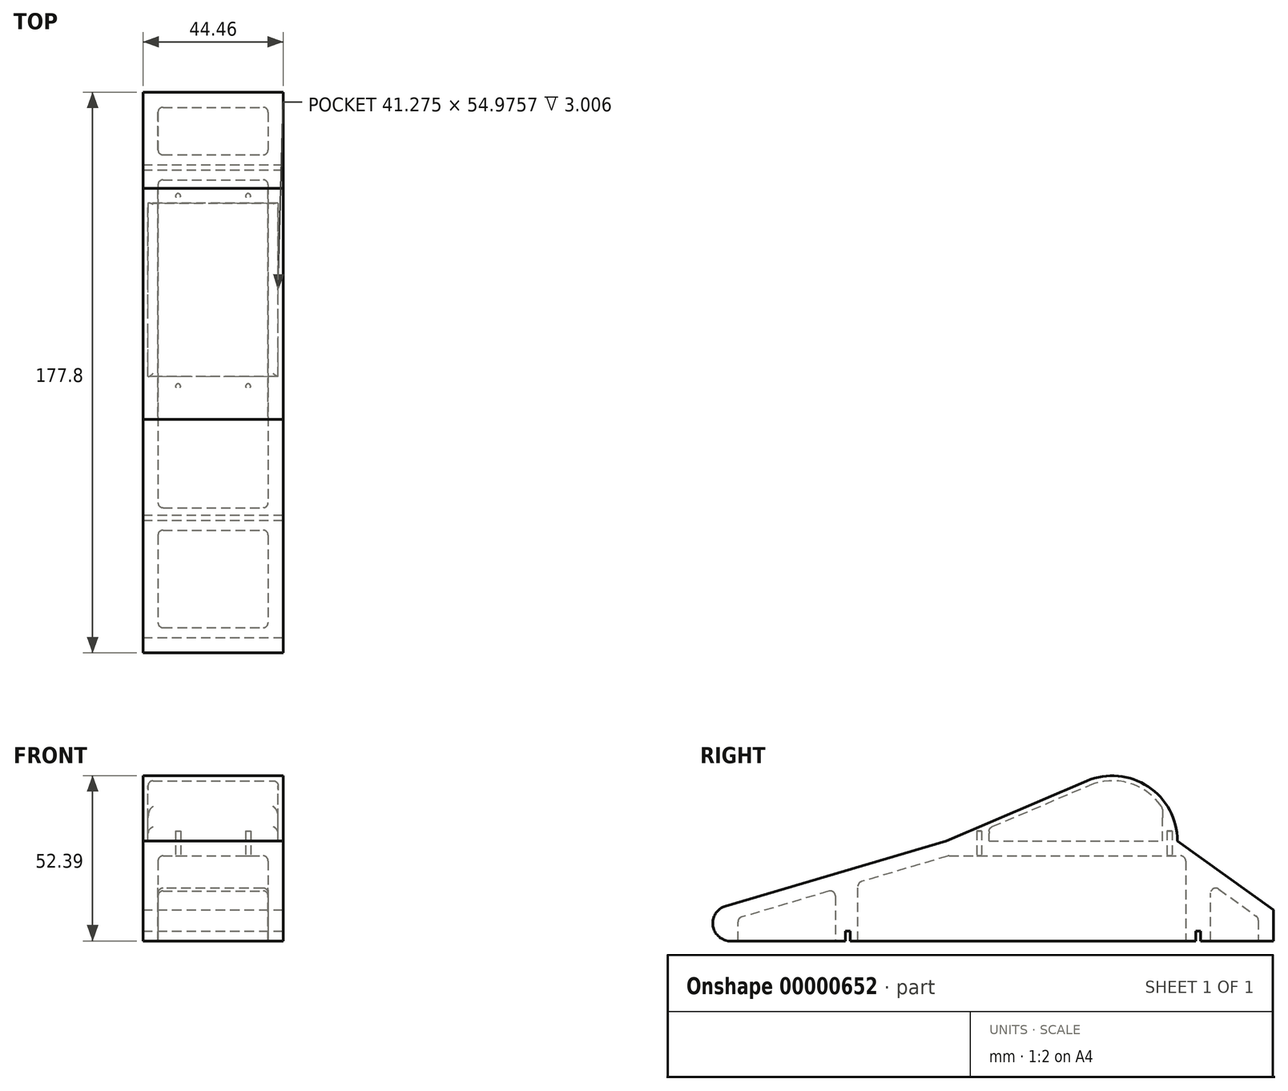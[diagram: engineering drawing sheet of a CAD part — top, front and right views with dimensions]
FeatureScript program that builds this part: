
annotation { "Feature Type Name" : "Feature", "Feature Type Description" : "" }
export const myFeature = defineFeature(function(context is Context, id is Id, definition is map)
    precondition{}
    {
        {
            var Q0;
            Q0=qCreatedBy(makeId("Right.planeOp"),FACE);
            var sketch = newSketch(context, id + "F0", { "sketchPlane" : qUnion([Q0])});
            skLineSegment(sketch, "E0.rect.bottom", {"start": v(-88.9, 15.88) * mm, "end": v(88.9, 15.88) * mm});
            skLineSegment(sketch, "E0.rect.top", {"start": v(-88.9, -15.88) * mm, "end": v(88.9, -15.88) * mm});
            skLineSegment(sketch, "E0.rect.left", {"start": v(-88.9, 15.88) * mm, "end": v(-88.9, -15.88) * mm});
            skLineSegment(sketch, "E0.rect.right", {"start": v(88.9, 15.88) * mm, "end": v(88.9, -15.88) * mm});
            skPoint(sketch, "E0.rect.middle", {"position": v(0, 0) * mm});
            skSolve(sketch);
        }
        {
            var Q0;
            Q0=makeQuery(id+"F0.imprint","IMPRINT",FACE,{"disambiguationData":[TD([[makeQuery(id+"F0.imprint","IMPRINT",EDGE,{"derivedFrom":sQuery(id+"F0.wireOp",EDGE,"E0.rect.bottom")}),-1.0]])]});
            extrude(context, id + "F1", {"entities" : qUnion([Q0]), "endBound" : BoundingType.SYMMETRIC, "depth" : 44.45 * mm});
        }
        {
            var Q0;
            Q0=qCreatedBy(makeId("Right.planeOp"),FACE);
            var sketch = newSketch(context, id + "F2", { "sketchPlane" : qUnion([Q0])});
            skLineSegment(sketch, "E1.bottom", {"start": v(-46.83, -15.88) * mm, "end": v(-45.24, -15.88) * mm});
            skLineSegment(sketch, "E1.top", {"start": v(-46.83, -12.7) * mm, "end": v(-45.24, -12.7) * mm});
            skLineSegment(sketch, "E1.left", {"start": v(-46.83, -15.87) * mm, "end": v(-46.83, -12.7) * mm});
            skLineSegment(sketch, "E1.right", {"start": v(-45.24, -15.87) * mm, "end": v(-45.24, -12.7) * mm});
            skLineSegment(sketch, "E2", {"start": v(-46.04, -12.7) * mm, "end": v(-46.04, -4.16) * mm, "construction": true});
            skLineSegment(sketch, "E3.bottom", {"start": v(64.3, -15.88) * mm, "end": v(65.88, -15.88) * mm});
            skLineSegment(sketch, "E3.top", {"start": v(64.3, -12.7) * mm, "end": v(65.88, -12.7) * mm});
            skLineSegment(sketch, "E3.left", {"start": v(64.3, -15.88) * mm, "end": v(64.3, -12.7) * mm});
            skLineSegment(sketch, "E3.right", {"start": v(65.88, -15.88) * mm, "end": v(65.88, -12.7) * mm});
            skCircle(sketch, "E4", {"center": v(-46.04, -13.7) * mm, "radius": 1 * mm, "construction": true});
            skCircle(sketch, "E5", {"center": v(65.09, -13.7) * mm, "radius": 1 * mm, "construction": true});
            skLineSegment(sketch, "E6", {"start": v(65.09, -13.7) * mm, "end": v(65.09, -12.7) * mm});
            skSolve(sketch);
        }
        {
            var Q0;
            {Q0=qUnion([makeQuery(id+"F2.imprint","IMPRINT",FACE,{"disambiguationData":[TD([[makeQuery(id+"F2.imprint","IMPRINT",EDGE,{"derivedFrom":sQuery(id+"F2.wireOp",EDGE,"E1.bottom")}),1.0]])]}),makeQuery(id+"F2.imprint","IMPRINT",FACE,{"disambiguationData":[TD([[makeQuery(id+"F2.imprint","IMPRINT",EDGE,{"derivedFrom":sQuery(id+"F2.wireOp",EDGE,"E3.bottom")}),1.0]])]})]);}
            extrude(context, id + "F3", {"entities" : qUnion([Q0]), "operationType" : NewBodyOperationType.REMOVE, "endBound" : BoundingType.SYMMETRIC, "oppositeDirection" : true, "depth" : 50.8 * mm});
        }
        {
            var Q0;
            Q0=qCreatedBy(makeId("Right.planeOp"),FACE);
            var sketch = newSketch(context, id + "F4", { "sketchPlane" : qUnion([Q0])});
            skLineSegment(sketch, "E7", {"start": v(-14.84, 15.88) * mm, "end": v(-84.87, -4.86) * mm});
            skArc(sketch, "E8", {"start": v(-84.87, -4.86) * mm, "mid": v(-88.9, -10.25) * mm, "end": v(-84.87, -15.64) * mm});
            skLineSegment(sketch, "E9", {"start": v(-14.84, 15.88) * mm, "end": v(-88.9, 15.88) * mm});
            skLineSegment(sketch, "E10", {"start": v(-88.9, 15.87) * mm, "end": v(-88.9, -15.88) * mm});
            skLineSegment(sketch, "E11", {"start": v(-84.87, -15.64) * mm, "end": v(-84.1, -15.88) * mm});
            skLineSegment(sketch, "E12", {"start": v(-84.1, -15.88) * mm, "end": v(-88.9, -15.88) * mm});
            skSolve(sketch);
        }
        {
            var Q0;
            Q0 = qSketchRegion(id + "F4", true);
            extrude(context, id + "F5", {"entities" : qUnion([Q0]), "operationType" : NewBodyOperationType.REMOVE, "endBound" : BoundingType.THROUGH_ALL, "oppositeDirection" : true, "depth" : 25.4 * mm, "hasSecondDirection" : true, "secondDirectionBound" : SecondDirectionBoundingType.THROUGH_ALL, "secondDirectionOppositeDirection" : false, "secondDirectionDepth" : 25.4 * mm});
        }
        {
            var Q0;
            Q0=qCreatedBy(makeId("Right.planeOp"),FACE);
            var sketch = newSketch(context, id + "F6", { "sketchPlane" : qUnion([Q0])});
            skLineSegment(sketch, "E13", {"start": v(58.47, 15.87) * mm, "end": v(88.9, -6.04) * mm});
            skLineSegment(sketch, "E14", {"start": v(58.47, 15.88) * mm, "end": v(88.9, 15.88) * mm});
            skLineSegment(sketch, "E15", {"start": v(88.9, 15.88) * mm, "end": v(88.9, -6.04) * mm});
            skSolve(sketch);
        }
        {
            var Q0;
            Q0 = qSketchRegion(id + "F6", true);
            extrude(context, id + "F7", {"entities" : qUnion([Q0]), "operationType" : NewBodyOperationType.REMOVE, "endBound" : BoundingType.THROUGH_ALL, "oppositeDirection" : true, "depth" : 25.4 * mm, "hasSecondDirection" : true, "secondDirectionBound" : SecondDirectionBoundingType.THROUGH_ALL, "secondDirectionOppositeDirection" : false, "secondDirectionDepth" : 25.4 * mm});
        }
        {
            var Q0;
            Q0=qCreatedBy(makeId("Right.planeOp"),FACE);
            var sketch = newSketch(context, id + "F8", { "sketchPlane" : qUnion([Q0])});
            skLineSegment(sketch, "E16", {"start": v(-14.15, 11.11) * mm, "end": v(61.12, 11.11) * mm});
            skLineSegment(sketch, "E17", {"start": v(61.12, 11.11) * mm, "end": v(61.12, -15.87) * mm});
            skLineSegment(sketch, "E18", {"start": v(61.12, -15.87) * mm, "end": v(-42.86, -15.88) * mm});
            skLineSegment(sketch, "E19", {"start": v(-42.86, -15.88) * mm, "end": v(-42.86, 2.61) * mm});
            skLineSegment(sketch, "E20", {"start": v(-50, 0.5) * mm, "end": v(-50, -15.88) * mm});
            skLineSegment(sketch, "E21", {"start": v(-50, -15.87) * mm, "end": v(-80.92, -15.88) * mm});
            skLineSegment(sketch, "E22.0", {"start": v(-14.15, 11.11) * mm, "end": v(-42.86, 2.61) * mm});
            skLineSegment(sketch, "E23.trimOffspring", {"start": v(-50, 0.5) * mm, "end": v(-80.92, -8.65) * mm});
            skLineSegment(sketch, "E24", {"start": v(-80.92, -15.88) * mm, "end": v(-80.92, -8.65) * mm});
            skLineSegment(sketch, "E25", {"start": v(69.06, 2.38) * mm, "end": v(84.14, -8.48) * mm});
            skLineSegment(sketch, "E26", {"start": v(84.14, -8.48) * mm, "end": v(84.14, -15.87) * mm});
            skLineSegment(sketch, "E27", {"start": v(84.14, -15.87) * mm, "end": v(69.06, -15.87) * mm});
            skLineSegment(sketch, "E28", {"start": v(69.06, -15.87) * mm, "end": v(69.06, 2.38) * mm});
            skPoint(sketch, "E29.orphan", {"position": v(72.36, 0) * mm});
            skSolve(sketch);
        }
        {
            var Q0;
            Q0 = qSketchRegion(id + "F8", true);
            extrude(context, id + "F9", {"entities" : qUnion([Q0]), "operationType" : NewBodyOperationType.REMOVE, "endBound" : BoundingType.SYMMETRIC, "oppositeDirection" : true, "depth" : 34.92 * mm});
        }
        {
            var Q0;
            Q0=makeQuery(id+"F9.boolean.opBoolean","COPY",FACE,{"derivedFrom":makeQuery(id+"F9.opExtrude","SWEPT_FACE",FACE,{"disambiguationData":[OSD([sQuery(id+"F8.wireOp",EDGE,"N0cLQH5f-bfhz-v5gN-91Li-IQNh1XUmvacc")])]})});
            var Q1;
            Q1=makeQuery(id+"F9.boolean.opBoolean","COPY",FACE,{"derivedFrom":makeQuery(id+"F9.opExtrude","SWEPT_FACE",FACE,{"disambiguationData":[OSD([sQuery(id+"F8.wireOp",EDGE,"E16")])]})});
            var Q2;
            Q2=makeQuery(id+"F9.boolean.opBoolean","COPY",FACE,{"derivedFrom":makeQuery(id+"F9.opExtrude","SWEPT_FACE",FACE,{"disambiguationData":[OSD([sQuery(id+"F8.wireOp",EDGE,"E22.0")])]})});
            var Q3;
            Q3=makeQuery(id+"F9.boolean.opBoolean","COPY",EDGE,{"derivedFrom":makeQuery(id+"F9.opExtrude","CAP_EDGE",EDGE,{"disambiguationData":[OSD([sQuery(id+"F8.wireOp",EDGE,"E17")])],"isStart":true})});
            var Q4;
            Q4=makeQuery(id+"F9.boolean.opBoolean","COPY",EDGE,{"derivedFrom":makeQuery(id+"F9.opExtrude","CAP_EDGE",EDGE,{"disambiguationData":[OSD([sQuery(id+"F8.wireOp",EDGE,"E17")])],"isStart":false})});
            var Q5;
            Q5=makeQuery(id+"F9.boolean.opBoolean","COPY",EDGE,{"derivedFrom":makeQuery(id+"F9.opExtrude","CAP_EDGE",EDGE,{"disambiguationData":[OSD([sQuery(id+"F8.wireOp",EDGE,"E19")])],"isStart":true})});
            var Q6;
            Q6=makeQuery(id+"F9.boolean.opBoolean","COPY",EDGE,{"derivedFrom":makeQuery(id+"F9.opExtrude","CAP_EDGE",EDGE,{"disambiguationData":[OSD([sQuery(id+"F8.wireOp",EDGE,"E19")])],"isStart":false})});
            var Q7;
            Q7=makeQuery(id+"F9.boolean.opBoolean","COPY",EDGE,{"derivedFrom":makeQuery(id+"F9.opExtrude","CAP_EDGE",EDGE,{"disambiguationData":[OSD([sQuery(id+"F8.wireOp",EDGE,"E24")])],"isStart":false})});
            var Q8;
            Q8=makeQuery(id+"F9.boolean.opBoolean","COPY",EDGE,{"derivedFrom":makeQuery(id+"F9.opExtrude","CAP_EDGE",EDGE,{"disambiguationData":[OSD([sQuery(id+"F8.wireOp",EDGE,"E24")])],"isStart":true})});
            var Q9;
            Q9=makeQuery(id+"F9.boolean.opBoolean","COPY",EDGE,{"derivedFrom":makeQuery(id+"F9.opExtrude","CAP_EDGE",EDGE,{"disambiguationData":[OSD([sQuery(id+"F8.wireOp",EDGE,"E20")])],"isStart":true})});
            var Q10;
            Q10=makeQuery(id+"F9.boolean.opBoolean","COPY",EDGE,{"derivedFrom":makeQuery(id+"F9.opExtrude","CAP_EDGE",EDGE,{"disambiguationData":[OSD([sQuery(id+"F8.wireOp",EDGE,"E20")])],"isStart":false})});
            var Q11;
            Q11=makeQuery(id+"F9.boolean.opBoolean","COPY",FACE,{"derivedFrom":makeQuery(id+"F9.opExtrude","SWEPT_FACE",FACE,{"disambiguationData":[OSD([sQuery(id+"F8.wireOp",EDGE,"E23.trimOffspring")])]})});
            var Q12;
            Q12=makeQuery(id+"F9.boolean.opBoolean","COPY",EDGE,{"derivedFrom":makeQuery(id+"F9.opExtrude","CAP_EDGE",EDGE,{"disambiguationData":[OSD([sQuery(id+"F8.wireOp",EDGE,"E28")])],"isStart":false})});
            var Q13;
            Q13=makeQuery(id+"F9.boolean.opBoolean","COPY",EDGE,{"derivedFrom":makeQuery(id+"F9.opExtrude","CAP_EDGE",EDGE,{"disambiguationData":[OSD([sQuery(id+"F8.wireOp",EDGE,"E28")])],"isStart":true})});
            var Q14;
            Q14=makeQuery(id+"F9.boolean.opBoolean","COPY",EDGE,{"derivedFrom":makeQuery(id+"F9.opExtrude","CAP_EDGE",EDGE,{"disambiguationData":[OSD([sQuery(id+"F8.wireOp",EDGE,"E26")])],"isStart":true})});
            var Q15;
            Q15=makeQuery(id+"F9.boolean.opBoolean","COPY",EDGE,{"derivedFrom":makeQuery(id+"F9.opExtrude","CAP_EDGE",EDGE,{"disambiguationData":[OSD([sQuery(id+"F8.wireOp",EDGE,"E26")])],"isStart":false})});
            var Q16;
            Q16=makeQuery(id+"F9.boolean.opBoolean","COPY",FACE,{"derivedFrom":makeQuery(id+"F9.opExtrude","SWEPT_FACE",FACE,{"disambiguationData":[OSD([sQuery(id+"F8.wireOp",EDGE,"E25")])]})});
            fillet(context, id + "F10", {"entities" : qUnion([Q0, Q1, Q2, Q3, Q4, Q5, Q6, Q7, Q8, Q9, Q10, Q11, Q12, Q13, Q14, Q15, Q16]), "radius" : 1.59 * mm, "tangentPropagation" : true, "allowEdgeOverflow" : false});
        }
        {
            var Q0;
            Q0=qCreatedBy(makeId("Right.planeOp"),FACE);
            var sketch = newSketch(context, id + "F11", { "sketchPlane" : qUnion([Q0])});
            skArc(sketch, "E30", {"start": v(29.75, 34.86) * mm, "mid": v(49.22, 33.1) * mm, "end": v(58.47, 15.88) * mm});
            skLineSegment(sketch, "E31", {"start": v(58.47, 15.88) * mm, "end": v(-14.84, 15.87) * mm});
            skPoint(sketch, "E32.visualSharp", {"position": v(17.95, 21.4) * mm});
            skLineSegment(sketch, "E33", {"start": v(29.75, 34.86) * mm, "end": v(-14.84, 15.87) * mm});
            skSolve(sketch);
        }
        {
            var Q0;
            Q0 = qSketchRegion(id + "F11", true);
            var Q1;
            Q1=makeQuery(id+"F1.opExtrude","CAP_FACE",FACE,{"disambiguationData":[OSD([sQuery(id+"F0.wireOp",EDGE,"E0.rect.bottom"),sQuery(id+"F0.wireOp",EDGE,"E0.rect.top"),sQuery(id+"F0.wireOp",EDGE,"E0.rect.left"),sQuery(id+"F0.wireOp",EDGE,"E0.rect.right")])],"isStart":true});
            var Q2;
            Q2=makeQuery(id+"F1.opExtrude","CAP_FACE",FACE,{"disambiguationData":[OSD([sQuery(id+"F0.wireOp",EDGE,"E0.rect.bottom"),sQuery(id+"F0.wireOp",EDGE,"E0.rect.top"),sQuery(id+"F0.wireOp",EDGE,"E0.rect.left"),sQuery(id+"F0.wireOp",EDGE,"E0.rect.right")])],"isStart":false});
            extrude(context, id + "F12", {"entities" : qUnion([Q0]), "endBound" : BoundingType.UP_TO_SURFACE, "oppositeDirection" : true, "endBoundEntityFace" : qUnion([Q1]), "depth" : 25.4 * mm, "hasSecondDirection" : true, "secondDirectionBound" : SecondDirectionBoundingType.UP_TO_SURFACE, "secondDirectionOppositeDirection" : false, "secondDirectionBoundEntityFace" : qUnion([Q2]), "secondDirectionDepth" : 25.4 * mm});
        }
        {
            var Q0;
            Q0=makeQuery(id+"F12.opExtrude","SWEPT_FACE",FACE,{"disambiguationData":[OSD([sQuery(id+"F11.wireOp",EDGE,"E31")])]});
            var Q1;
            Q1=makeQuery(id+"F12.opExtrude","SWEPT_BODY",BODY,{"disambiguationData":[OSD([sQuery(id+"F11.wireOp",EDGE,"7nJv536j-TVK7-uIK1-10eV-QeMPr05hsf2R"),sQuery(id+"F11.wireOp",EDGE,"E30"),sQuery(id+"F11.wireOp",EDGE,"E31")])]});
            shell(context, id + "F13", {"entities" : qUnion([Q0]), "parts" : qUnion([Q1]), "thickness" : 1.59 * mm});
        }
        {
            var Q0;
            Q0=qCreatedBy(makeId("Right.planeOp"),FACE);
            var sketch = newSketch(context, id + "F14", { "sketchPlane" : qUnion([Q0])});
            skLineSegment(sketch, "E34", {"start": v(-10.8, 15.87) * mm, "end": v(-1.27, 15.87) * mm});
            skLineSegment(sketch, "E35", {"start": v(-1.27, 15.87) * mm, "end": v(-1.27, 19.93) * mm});
            skLineSegment(sketch, "E36", {"start": v(-1.27, 19.93) * mm, "end": v(-10.8, 15.87) * mm});
            skLineSegment(sketch, "E37", {"start": v(56.89, 15.88) * mm, "end": v(53.71, 15.88) * mm});
            skLineSegment(sketch, "E38", {"start": v(53.71, 15.88) * mm, "end": v(53.71, 26.4) * mm});
            skArc(sketch, "E39.0", {"start": v(56.89, 15.88) * mm, "mid": v(56.07, 21.37) * mm, "end": v(53.71, 26.4) * mm});
            skPoint(sketch, "E40.orphan", {"position": v(30.37, 33.4) * mm});
            skSolve(sketch);
        }
        {
            var Q0;
            Q0 = qSketchRegion(id + "F14", true);
            var Q1;
            {var subQ0=sQuery(id+"F11.wireOp",EDGE,"E33");var subQ1=sQuery(id+"F11.wireOp",EDGE,"E31");var subQ2=sQuery(id+"F11.wireOp",EDGE,"E30");Q1=makeQuery(id+"F13.opShell","OFFSET_FACE",FACE,{"disambiguationData":[OSD([subQ2,subQ1,subQ0]),TDD([makeQuery(id+"F12.opExtrude","CAP_FACE",FACE,{"disambiguationData":[OSD([subQ2,subQ1,subQ0])],"isStart":true})])]});}
            var Q2;
            {var subQ0=sQuery(id+"F11.wireOp",EDGE,"E33");var subQ1=sQuery(id+"F11.wireOp",EDGE,"E31");var subQ2=sQuery(id+"F11.wireOp",EDGE,"E30");Q2=makeQuery(id+"F13.opShell","OFFSET_FACE",FACE,{"disambiguationData":[OSD([subQ2,subQ1,subQ0]),TDD([makeQuery(id+"F12.opExtrude","CAP_FACE",FACE,{"disambiguationData":[OSD([subQ2,subQ1,subQ0])],"isStart":false})])]});}
            extrude(context, id + "F15", {"entities" : qUnion([Q0]), "operationType" : NewBodyOperationType.ADD, "endBound" : BoundingType.UP_TO_SURFACE, "endBoundEntityFace" : qUnion([Q1]), "depth" : 25.4 * mm, "hasSecondDirection" : true, "secondDirectionBound" : SecondDirectionBoundingType.UP_TO_SURFACE, "secondDirectionOppositeDirection" : true, "secondDirectionBoundEntityFace" : qUnion([Q2]), "secondDirectionDepth" : 25.4 * mm});
        }
        {
            var Q0;
            Q0=makeQuery(id+"F9.boolean.opBoolean","COPY",FACE,{"derivedFrom":makeQuery(id+"F9.opExtrude","SWEPT_FACE",FACE,{"disambiguationData":[OSD([sQuery(id+"F8.wireOp",EDGE,"E16")])]})});
            var sketch = newSketch(context, id + "F16", { "sketchPlane" : qUnion([Q0])});
            skCircle(sketch, "E41", {"center": v(11.11, 4.4) * mm, "radius": 0.8 * mm});
            skCircle(sketch, "E42", {"center": v(-11.11, 4.4) * mm, "radius": 0.8 * mm});
            skCircle(sketch, "E43", {"center": v(11.11, -55.96) * mm, "radius": 0.8 * mm});
            skCircle(sketch, "E44", {"center": v(-11.11, -55.96) * mm, "radius": 0.8 * mm});
            skLineSegment(sketch, "E45.bottom", {"start": v(11.11, 4.4) * mm, "end": v(-11.11, 4.4) * mm, "construction": true});
            skLineSegment(sketch, "E45.top", {"start": v(11.11, -55.96) * mm, "end": v(-11.11, -55.96) * mm, "construction": true});
            skLineSegment(sketch, "E45.left", {"start": v(11.11, 4.4) * mm, "end": v(11.11, -55.96) * mm, "construction": true});
            skLineSegment(sketch, "E45.right", {"start": v(-11.11, 4.4) * mm, "end": v(-11.11, -55.96) * mm, "construction": true});
            skSolve(sketch);
        }
        {
            var Q0;
            Q0 = qSketchRegion(id + "F16", true);
            extrude(context, id + "F17", {"entities" : qUnion([Q0]), "operationType" : NewBodyOperationType.REMOVE, "oppositeDirection" : true, "depth" : 7.94 * mm});
        }
        {
            var Q0;
            Q0=makeQuery(id+"F13.opShell","OFFSET_FACE",FACE,{"disambiguationData":[OSD([sQuery(id+"F11.wireOp",EDGE,"E33")])]});
            var Q1;
            Q1=makeQuery(id+"F13.opShell","OFFSET_FACE",FACE,{"disambiguationData":[OSD([sQuery(id+"F11.wireOp",EDGE,"E30")])]});
            var Q2;
            Q2=makeQuery(id+"F15.opExtrude","CAP_EDGE",EDGE,{"disambiguationData":[OSD([sQuery(id+"F14.wireOp",EDGE,"E38")])],"isStart":false});
            var Q3;
            Q3=makeQuery(id+"F15.opExtrude","CAP_EDGE",EDGE,{"disambiguationData":[OSD([sQuery(id+"F14.wireOp",EDGE,"E38")])],"isStart":true});
            var Q4;
            Q4=makeQuery(id+"F15.opExtrude","CAP_EDGE",EDGE,{"disambiguationData":[OSD([sQuery(id+"F14.wireOp",EDGE,"E35")])],"isStart":false});
            var Q5;
            Q5=makeQuery(id+"F15.opExtrude","CAP_EDGE",EDGE,{"disambiguationData":[OSD([sQuery(id+"F14.wireOp",EDGE,"E35")])],"isStart":true});
            fillet(context, id + "F18", {"entities" : qUnion([Q0, Q1, Q2, Q3, Q4, Q5]), "radius" : 1.59 * mm, "tangentPropagation" : true, "allowEdgeOverflow" : false});
        }
    });
